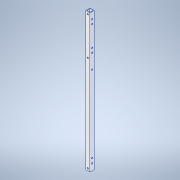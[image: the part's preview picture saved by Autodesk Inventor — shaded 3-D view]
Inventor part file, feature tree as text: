
AUTODESK INVENTOR PART (.ipt)
format: ipt  version: 2020.3 (Build 243373000, 373)  size: 172,544 bytes
history: native  units: mm
features: sketch x9, hole x8, other x1, extrude x1
ambient origin geometry x8: Origin, YZ Plane, XZ Plane, XY Plane, X Axis, Y Axis, Z Axis, Center Point
bodies: Body1 (feature_tree)
feature tree (19):
  other  "ソリッド1"
  extrude  "押し出し1"  Depth=9.0mm
  hole  "穴1"  [1 undecoded]
  hole  "穴2"  [1 undecoded]
  hole  "穴3"  [1 undecoded]
  hole  "穴4"  [1 undecoded]
  hole  "穴5"  [1 undecoded]
  hole  "穴6"  [1 undecoded]
  hole  "穴7"  [1 undecoded]
  hole  "穴8"  [1 undecoded]
  sketch  "スケッチ1"
  sketch  "スケッチ2"
  sketch  "スケッチ3"
  sketch  "スケッチ4"
  sketch  "スケッチ5"
  sketch  "スケッチ6"
  sketch  "スケッチ7"
  sketch  "スケッチ8"
  sketch  "スケッチ9"
note: 8 required parameter values undecoded (feature->parameter linkage not recoverable at this tier; creation-order binding heuristic only, values carry confidence <= 0.55)
